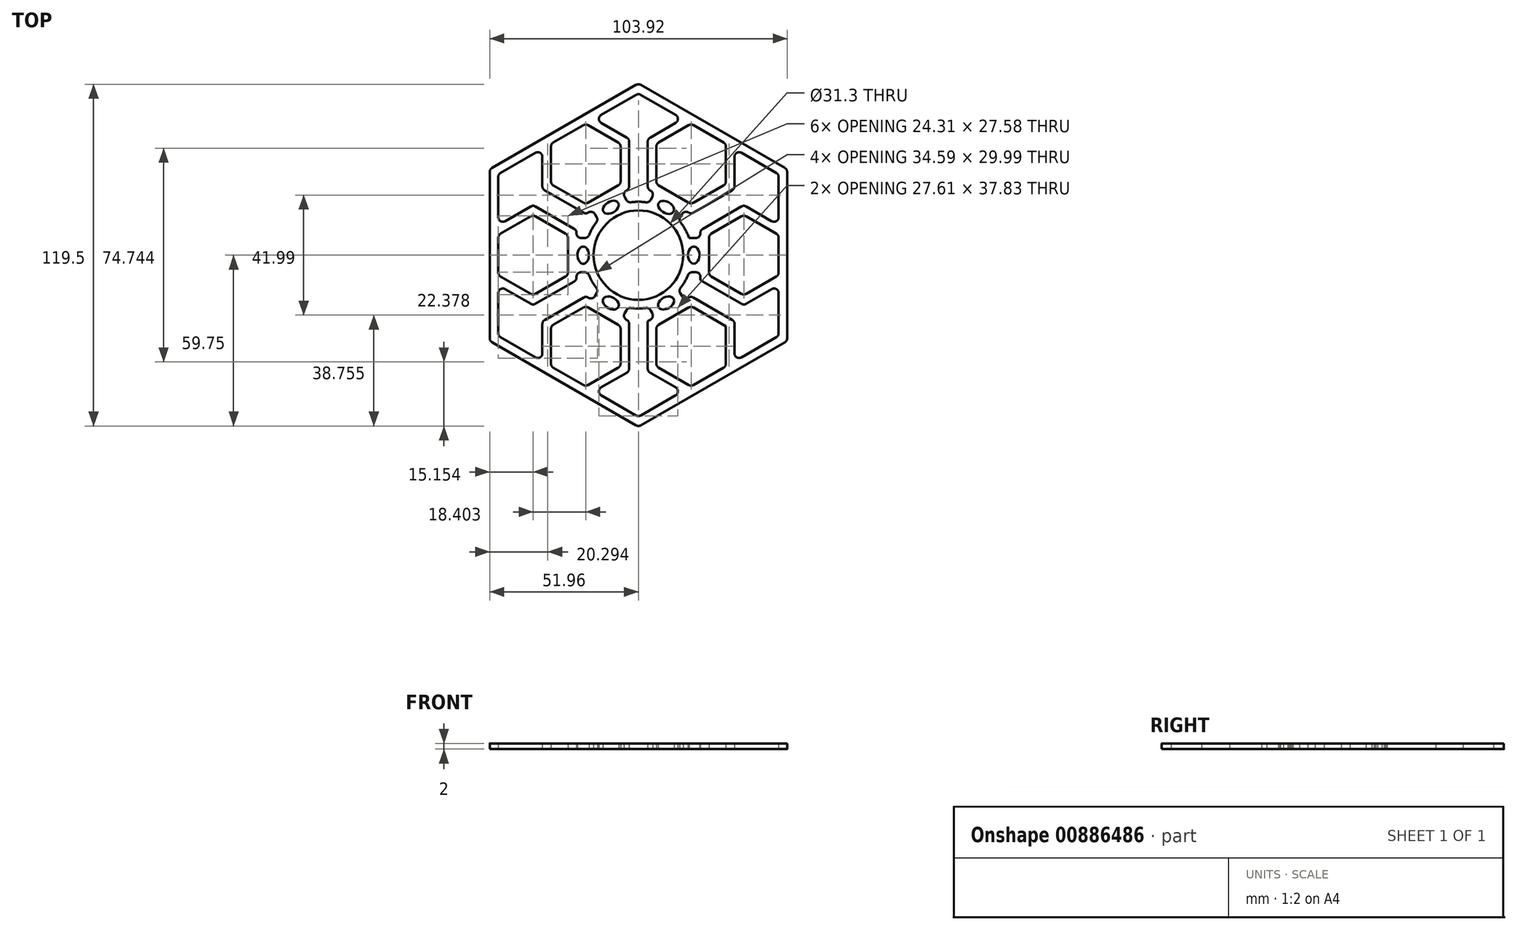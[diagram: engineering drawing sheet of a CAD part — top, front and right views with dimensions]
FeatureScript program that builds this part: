
annotation { "Feature Type Name" : "Feature", "Feature Type Description" : "" }
export const myFeature = defineFeature(function(context is Context, id is Id, definition is map)
    precondition{}
    {
        {
            var Q0;
            Q0=qCreatedBy(makeId("Top.planeOp"),FACE);
            var sketch = newSketch(context, id + "F0", { "sketchPlane" : qUnion([Q0])});
            skCircle(sketch, "E0.cCircle", {"center": v(0, 0) * mm, "radius": 60 * mm, "construction": true});
            skLineSegment(sketch, "E0.0", {"start": v(0, -60) * mm, "end": v(-51.96, -30) * mm});
            skLineSegment(sketch, "E0.1", {"start": v(-51.96, -30) * mm, "end": v(-51.96, 30) * mm});
            skLineSegment(sketch, "E0.2", {"start": v(-51.96, 30) * mm, "end": v(0, 60) * mm});
            skLineSegment(sketch, "E0.3", {"start": v(0, 60) * mm, "end": v(51.96, 30) * mm});
            skLineSegment(sketch, "E0.4", {"start": v(51.96, 30) * mm, "end": v(51.96, -30) * mm});
            skLineSegment(sketch, "E0.5", {"start": v(51.96, -30) * mm, "end": v(0, -60) * mm});
            skCircle(sketch, "E1.cCircle", {"center": v(0, 0) * mm, "radius": 56.54 * mm, "construction": true});
            skLineSegment(sketch, "E1.0", {"start": v(0, -56.54) * mm, "end": v(-15.4, -47.64) * mm});
            skLineSegment(sketch, "E1.1", {"start": v(-48.96, -28.27) * mm, "end": v(-48.96, 28.27) * mm});
            skLineSegment(sketch, "E1.2", {"start": v(-48.96, 28.27) * mm, "end": v(-18.4, 45.91) * mm});
            skLineSegment(sketch, "E1.3", {"start": v(0, 56.54) * mm, "end": v(15.4, 47.64) * mm});
            skLineSegment(sketch, "E1.4", {"start": v(48.96, 28.27) * mm, "end": v(48.96, 10.48) * mm});
            skLineSegment(sketch, "E1.5", {"start": v(48.96, -28.27) * mm, "end": v(33.56, -37.16) * mm});
            skCircle(sketch, "E2.cCircle", {"center": v(-36.8, 0) * mm, "radius": 17.5 * mm, "construction": true});
            skLineSegment(sketch, "E2.0", {"start": v(-51.96, -8.75) * mm, "end": v(-51.96, 8.75) * mm});
            skLineSegment(sketch, "E2.1", {"start": v(-48.96, 10.48) * mm, "end": v(-36.8, 17.5) * mm});
            skLineSegment(sketch, "E2.2", {"start": v(-36.8, 17.5) * mm, "end": v(-21.65, 8.75) * mm});
            skLineSegment(sketch, "E2.3", {"start": v(-21.65, 8.75) * mm, "end": v(-21.65, 6) * mm});
            skLineSegment(sketch, "E2.4", {"start": v(-21.65, -8.75) * mm, "end": v(-36.8, -17.5) * mm});
            skLineSegment(sketch, "E2.5", {"start": v(-36.8, -17.5) * mm, "end": v(-48.96, -10.48) * mm});
            skCircle(sketch, "E3.cCircle", {"center": v(-36.8, 0) * mm, "radius": 14.04 * mm, "construction": true});
            skLineSegment(sketch, "E3.0", {"start": v(-36.8, -14.04) * mm, "end": v(-48.96, -7.02) * mm});
            skLineSegment(sketch, "E3.1", {"start": v(-48.96, -7.02) * mm, "end": v(-48.96, 7.02) * mm});
            skLineSegment(sketch, "E3.2", {"start": v(-48.96, 7.02) * mm, "end": v(-36.8, 14.04) * mm});
            skLineSegment(sketch, "E3.3", {"start": v(-36.8, 14.04) * mm, "end": v(-24.65, 7.02) * mm});
            skLineSegment(sketch, "E3.4", {"start": v(-24.65, 7.02) * mm, "end": v(-24.65, -7.02) * mm});
            skLineSegment(sketch, "E3.5", {"start": v(-24.65, -7.02) * mm, "end": v(-36.8, -14.04) * mm});
            skArc(sketch, "E4", {"start": v(-17.66, -6) * mm, "mid": v(-16.15, -9.33) * mm, "end": v(-14.03, -12.3) * mm});
            skCircle(sketch, "E5", {"center": v(0, 0) * mm, "radius": 15.65 * mm});
            skLineSegment(sketch, "E6", {"start": v(-21.65, -6) * mm, "end": v(-17.66, -6) * mm});
            skLineSegment(sketch, "E7", {"start": v(-21.65, 6) * mm, "end": v(-17.66, 6) * mm});
            skLineSegment(sketch, "E8.trimOffspring", {"start": v(-21.65, -6) * mm, "end": v(-21.65, -8.75) * mm});
            skEllipse(sketch, "E9", {"center": v(-19.3, 0) * mm, "majorRadius": 3 * mm, "minorRadius": 2 * mm, "majorAxis": v(0, 1)});
            skLineSegment(sketch, "E10.1.0", {"start": v(-5.63, -21.75) * mm, "end": v(-3.25, -23.12) * mm});
            skLineSegment(sketch, "E10.1.1", {"start": v(-5.63, -21.75) * mm, "end": v(-3.63, -18.3) * mm});
            skLineSegment(sketch, "E10.1.2", {"start": v(-3.25, -23.12) * mm, "end": v(-3.25, -40.63) * mm});
            skLineSegment(sketch, "E10.1.3", {"start": v(-3.25, -40.62) * mm, "end": v(-15.4, -47.64) * mm});
            skLineSegment(sketch, "E10.1.4", {"start": v(-6.25, -38.9) * mm, "end": v(-18.4, -45.91) * mm});
            skLineSegment(sketch, "E10.1.5", {"start": v(-30.56, -38.9) * mm, "end": v(-30.56, -24.86) * mm});
            skLineSegment(sketch, "E10.1.6", {"start": v(-30.56, -24.86) * mm, "end": v(-18.4, -17.84) * mm});
            skLineSegment(sketch, "E10.1.7", {"start": v(-18.4, -17.84) * mm, "end": v(-6.25, -24.86) * mm});
            skLineSegment(sketch, "E10.1.8", {"start": v(-6.25, -24.86) * mm, "end": v(-6.25, -38.9) * mm});
            skLineSegment(sketch, "E10.1.9", {"start": v(-18.4, -14.37) * mm, "end": v(-16.02, -15.75) * mm});
            skLineSegment(sketch, "E10.1.10", {"start": v(-33.56, -23.12) * mm, "end": v(-18.4, -14.38) * mm});
            skLineSegment(sketch, "E10.1.11", {"start": v(-33.56, -37.16) * mm, "end": v(-33.56, -23.12) * mm});
            skLineSegment(sketch, "E10.1.12", {"start": v(-16.02, -15.75) * mm, "end": v(-14.03, -12.3) * mm});
            skEllipse(sketch, "E10.1.13", {"center": v(-9.65, -16.72) * mm, "majorRadius": 3 * mm, "minorRadius": 2 * mm, "majorAxis": v(-0.87, 0.5)});
            skLineSegment(sketch, "E10.2.0", {"start": v(16.02, -15.75) * mm, "end": v(18.4, -14.38) * mm});
            skLineSegment(sketch, "E10.2.1", {"start": v(16.02, -15.75) * mm, "end": v(14.03, -12.3) * mm});
            skLineSegment(sketch, "E10.2.2", {"start": v(18.4, -14.38) * mm, "end": v(33.56, -23.13) * mm});
            skLineSegment(sketch, "E10.2.3", {"start": v(33.56, -23.13) * mm, "end": v(33.56, -37.16) * mm});
            skLineSegment(sketch, "E10.2.4", {"start": v(30.56, -24.86) * mm, "end": v(30.56, -38.9) * mm});
            skLineSegment(sketch, "E10.2.5", {"start": v(18.4, -45.91) * mm, "end": v(6.25, -38.9) * mm});
            skLineSegment(sketch, "E10.2.6", {"start": v(6.25, -38.9) * mm, "end": v(6.25, -24.86) * mm});
            skLineSegment(sketch, "E10.2.7", {"start": v(6.25, -24.86) * mm, "end": v(18.4, -17.84) * mm});
            skLineSegment(sketch, "E10.2.8", {"start": v(18.4, -17.84) * mm, "end": v(30.56, -24.86) * mm});
            skLineSegment(sketch, "E10.2.9", {"start": v(3.25, -23.13) * mm, "end": v(5.63, -21.75) * mm});
            skLineSegment(sketch, "E10.2.10", {"start": v(3.25, -40.62) * mm, "end": v(3.25, -23.13) * mm});
            skLineSegment(sketch, "E10.2.11", {"start": v(15.4, -47.64) * mm, "end": v(3.25, -40.63) * mm});
            skLineSegment(sketch, "E10.2.12", {"start": v(5.63, -21.75) * mm, "end": v(3.63, -18.3) * mm});
            skEllipse(sketch, "E10.2.13", {"center": v(9.65, -16.72) * mm, "majorRadius": 3 * mm, "minorRadius": 2 * mm, "majorAxis": v(-0.87, -0.5)});
            skLineSegment(sketch, "E10.3.0", {"start": v(21.65, 6) * mm, "end": v(21.65, 8.75) * mm});
            skLineSegment(sketch, "E10.3.1", {"start": v(21.65, 6) * mm, "end": v(17.66, 6) * mm});
            skLineSegment(sketch, "E10.3.2", {"start": v(21.65, 8.75) * mm, "end": v(36.8, 17.5) * mm});
            skLineSegment(sketch, "E10.3.3", {"start": v(36.8, 17.5) * mm, "end": v(48.96, 10.48) * mm});
            skLineSegment(sketch, "E10.3.4", {"start": v(36.8, 14.04) * mm, "end": v(48.96, 7.02) * mm});
            skLineSegment(sketch, "E10.3.5", {"start": v(48.96, -7.02) * mm, "end": v(36.8, -14.04) * mm});
            skLineSegment(sketch, "E10.3.6", {"start": v(36.8, -14.04) * mm, "end": v(24.65, -7.02) * mm});
            skLineSegment(sketch, "E10.3.7", {"start": v(24.65, -7.02) * mm, "end": v(24.65, 7.02) * mm});
            skLineSegment(sketch, "E10.3.8", {"start": v(24.65, 7.02) * mm, "end": v(36.8, 14.04) * mm});
            skLineSegment(sketch, "E10.3.9", {"start": v(21.65, -8.75) * mm, "end": v(21.65, -6) * mm});
            skLineSegment(sketch, "E10.3.10", {"start": v(36.8, -17.5) * mm, "end": v(21.65, -8.75) * mm});
            skLineSegment(sketch, "E10.3.11", {"start": v(48.96, -10.48) * mm, "end": v(36.8, -17.5) * mm});
            skLineSegment(sketch, "E10.3.12", {"start": v(21.65, -6) * mm, "end": v(17.66, -6) * mm});
            skEllipse(sketch, "E10.3.13", {"center": v(19.3, 0) * mm, "majorRadius": 3 * mm, "minorRadius": 2 * mm, "majorAxis": v(0, -1)});
            skLineSegment(sketch, "E10.4.0", {"start": v(5.63, 21.75) * mm, "end": v(3.25, 23.12) * mm});
            skLineSegment(sketch, "E10.4.1", {"start": v(5.63, 21.75) * mm, "end": v(3.63, 18.3) * mm});
            skLineSegment(sketch, "E10.4.2", {"start": v(3.25, 23.12) * mm, "end": v(3.25, 40.62) * mm});
            skLineSegment(sketch, "E10.4.3", {"start": v(3.25, 40.62) * mm, "end": v(15.4, 47.64) * mm});
            skLineSegment(sketch, "E10.4.4", {"start": v(6.25, 38.9) * mm, "end": v(18.4, 45.91) * mm});
            skLineSegment(sketch, "E10.4.5", {"start": v(30.56, 38.9) * mm, "end": v(30.56, 24.86) * mm});
            skLineSegment(sketch, "E10.4.6", {"start": v(30.56, 24.86) * mm, "end": v(18.4, 17.84) * mm});
            skLineSegment(sketch, "E10.4.7", {"start": v(18.4, 17.84) * mm, "end": v(6.25, 24.86) * mm});
            skLineSegment(sketch, "E10.4.8", {"start": v(6.25, 24.86) * mm, "end": v(6.25, 38.9) * mm});
            skLineSegment(sketch, "E10.4.9", {"start": v(18.4, 14.37) * mm, "end": v(16.02, 15.75) * mm});
            skLineSegment(sketch, "E10.4.10", {"start": v(33.56, 23.12) * mm, "end": v(18.4, 14.37) * mm});
            skLineSegment(sketch, "E10.4.11", {"start": v(33.56, 37.16) * mm, "end": v(33.56, 23.12) * mm});
            skLineSegment(sketch, "E10.4.12", {"start": v(16.02, 15.75) * mm, "end": v(14.03, 12.3) * mm});
            skEllipse(sketch, "E10.4.13", {"center": v(9.65, 16.72) * mm, "majorRadius": 3 * mm, "minorRadius": 2 * mm, "majorAxis": v(0.87, -0.5)});
            skLineSegment(sketch, "E10.5.0", {"start": v(-16.02, 15.75) * mm, "end": v(-18.4, 14.38) * mm});
            skLineSegment(sketch, "E10.5.1", {"start": v(-16.02, 15.75) * mm, "end": v(-14.03, 12.3) * mm});
            skLineSegment(sketch, "E10.5.2", {"start": v(-18.4, 14.38) * mm, "end": v(-33.56, 23.12) * mm});
            skLineSegment(sketch, "E10.5.3", {"start": v(-33.56, 23.12) * mm, "end": v(-33.56, 40.62) * mm});
            skLineSegment(sketch, "E10.5.4", {"start": v(-30.56, 24.86) * mm, "end": v(-30.56, 38.9) * mm});
            skLineSegment(sketch, "E10.5.5", {"start": v(-18.4, 45.91) * mm, "end": v(-6.25, 38.9) * mm});
            skLineSegment(sketch, "E10.5.6", {"start": v(-6.25, 38.9) * mm, "end": v(-6.25, 24.86) * mm});
            skLineSegment(sketch, "E10.5.7", {"start": v(-6.25, 24.86) * mm, "end": v(-18.4, 17.84) * mm});
            skLineSegment(sketch, "E10.5.8", {"start": v(-18.4, 17.84) * mm, "end": v(-30.56, 24.86) * mm});
            skLineSegment(sketch, "E10.5.9", {"start": v(-3.25, 23.13) * mm, "end": v(-5.63, 21.75) * mm});
            skLineSegment(sketch, "E10.5.10", {"start": v(-3.25, 40.63) * mm, "end": v(-3.25, 23.13) * mm});
            skLineSegment(sketch, "E10.5.11", {"start": v(-15.4, 47.64) * mm, "end": v(-3.25, 40.62) * mm});
            skLineSegment(sketch, "E10.5.12", {"start": v(-5.63, 21.75) * mm, "end": v(-3.63, 18.3) * mm});
            skEllipse(sketch, "E10.5.13", {"center": v(-9.65, 16.72) * mm, "majorRadius": 3 * mm, "minorRadius": 2 * mm, "majorAxis": v(0.87, 0.5)});
            skLineSegment(sketch, "E11.trimOffspring", {"start": v(-33.56, -37.16) * mm, "end": v(-48.96, -28.27) * mm});
            skPoint(sketch, "E12.orphan", {"position": v(-33.56, -40.62) * mm});
            skPoint(sketch, "E13.orphan", {"position": v(-18.4, -49.37) * mm});
            skLineSegment(sketch, "E14.trimOffspring", {"start": v(-18.4, -45.91) * mm, "end": v(-30.56, -38.9) * mm});
            skPoint(sketch, "E15.orphan", {"position": v(18.4, -49.38) * mm});
            skLineSegment(sketch, "E16.trimOffspring", {"start": v(15.4, -47.64) * mm, "end": v(0, -56.54) * mm});
            skLineSegment(sketch, "E17.trimOffspring", {"start": v(30.56, -38.9) * mm, "end": v(18.4, -45.91) * mm});
            skPoint(sketch, "E18.orphan", {"position": v(33.56, -40.63) * mm});
            skArc(sketch, "E19.trimOffspring", {"start": v(-14.03, 12.3) * mm, "mid": v(-16.15, 9.33) * mm, "end": v(-17.66, 6) * mm});
            skArc(sketch, "E20.trimOffspring", {"start": v(3.63, 18.3) * mm, "mid": v(0, 18.65) * mm, "end": v(-3.63, 18.3) * mm});
            skArc(sketch, "E21.trimOffspring", {"start": v(17.66, 6) * mm, "mid": v(16.15, 9.33) * mm, "end": v(14.03, 12.3) * mm});
            skArc(sketch, "E22.trimOffspring", {"start": v(14.03, -12.3) * mm, "mid": v(16.15, -9.33) * mm, "end": v(17.66, -6) * mm});
            skArc(sketch, "E23.trimOffspring", {"start": v(-3.63, -18.3) * mm, "mid": v(1.7, -18.57) * mm, "end": v(6.88, -17.34) * mm});
            skLineSegment(sketch, "E24.trimOffspring", {"start": v(-15.4, 47.64) * mm, "end": v(0, 56.54) * mm});
            skPoint(sketch, "E25.orphan", {"position": v(-18.4, 49.37) * mm});
            skPoint(sketch, "E26.orphan", {"position": v(18.4, 49.37) * mm});
            skLineSegment(sketch, "E27.trimOffspring", {"start": v(18.4, 45.91) * mm, "end": v(30.56, 38.9) * mm});
            skLineSegment(sketch, "E28.trimOffspring", {"start": v(33.56, 37.16) * mm, "end": v(48.96, 28.27) * mm});
            skPoint(sketch, "E29.orphan", {"position": v(33.56, 40.62) * mm});
            skPoint(sketch, "E30.orphan", {"position": v(51.96, 8.75) * mm});
            skLineSegment(sketch, "E31.trimOffspring", {"start": v(48.96, 7.02) * mm, "end": v(48.96, -7.02) * mm});
            skPoint(sketch, "E32.orphan", {"position": v(51.96, -8.75) * mm});
            skLineSegment(sketch, "E33.trimOffspring", {"start": v(48.96, -10.48) * mm, "end": v(48.96, -28.27) * mm});
            skSolve(sketch);
        }
        {
            var Q0;
            {var subQ16=sQuery(id+"F0.wireOp",EDGE,"E0.0");Q0=makeQuery(id+"F0.imprint","IMPRINT",FACE,{"disambiguationData":[TD([[makeQuery(id+"F0.imprint","IMPRINT",EDGE,{"derivedFrom":subQ16}),-1.0]])]});}
            extrude(context, id + "F1", {"entities" : qUnion([Q0]), "depth" : 2 * mm, "offsetDistance" : 25 * mm});
        }
        {
            var Q0;
            Q0=makeQuery(id+"F1.opExtrude","SWEPT_EDGE",EDGE,{"disambiguationData":[OSD([sQuery(id+"F0.wireOp",EDGE,"E6"),sQuery(id+"F0.wireOp",EDGE,"E8.trimOffspring")])]});
            var Q1;
            Q1=makeQuery(id+"F1.opExtrude","SWEPT_EDGE",EDGE,{"disambiguationData":[OSD([sQuery(id+"F0.wireOp",EDGE,"E10.2.1"),sQuery(id+"F0.wireOp",EDGE,"E22.trimOffspring")])]});
            var Q2;
            Q2=makeQuery(id+"F1.opExtrude","SWEPT_EDGE",EDGE,{"disambiguationData":[OSD([sQuery(id+"F0.wireOp",EDGE,"E10.4.12"),sQuery(id+"F0.wireOp",EDGE,"E21.trimOffspring")])]});
            var Q3;
            Q3=makeQuery(id+"F1.opExtrude","SWEPT_EDGE",EDGE,{"disambiguationData":[OSD([sQuery(id+"F0.wireOp",EDGE,"E10.5.9"),sQuery(id+"F0.wireOp",EDGE,"E10.5.12")])]});
            var Q4;
            Q4=makeQuery(id+"F1.opExtrude","SWEPT_EDGE",EDGE,{"disambiguationData":[OSD([sQuery(id+"F0.wireOp",EDGE,"E10.3.12"),sQuery(id+"F0.wireOp",EDGE,"E22.trimOffspring")])]});
            var Q5;
            Q5=makeQuery(id+"F1.opExtrude","SWEPT_EDGE",EDGE,{"disambiguationData":[OSD([sQuery(id+"F0.wireOp",EDGE,"E10.5.0"),sQuery(id+"F0.wireOp",EDGE,"E10.5.1")])]});
            var Q6;
            Q6=makeQuery(id+"F1.opExtrude","SWEPT_EDGE",EDGE,{"disambiguationData":[OSD([sQuery(id+"F0.wireOp",EDGE,"E2.3"),sQuery(id+"F0.wireOp",EDGE,"E7")])]});
            var Q7;
            Q7=makeQuery(id+"F1.opExtrude","SWEPT_EDGE",EDGE,{"disambiguationData":[OSD([sQuery(id+"F0.wireOp",EDGE,"E10.1.9"),sQuery(id+"F0.wireOp",EDGE,"E10.1.12")])]});
            var Q8;
            Q8=makeQuery(id+"F1.opExtrude","SWEPT_EDGE",EDGE,{"disambiguationData":[OSD([sQuery(id+"F0.wireOp",EDGE,"E10.4.1"),sQuery(id+"F0.wireOp",EDGE,"E20.trimOffspring")])]});
            var Q9;
            Q9=makeQuery(id+"F1.opExtrude","SWEPT_EDGE",EDGE,{"disambiguationData":[OSD([sQuery(id+"F0.wireOp",EDGE,"E10.5.1"),sQuery(id+"F0.wireOp",EDGE,"E19.trimOffspring")])]});
            var Q10;
            Q10=makeQuery(id+"F1.opExtrude","SWEPT_EDGE",EDGE,{"disambiguationData":[OSD([sQuery(id+"F0.wireOp",EDGE,"E7"),sQuery(id+"F0.wireOp",EDGE,"E19.trimOffspring")])]});
            var Q11;
            Q11=makeQuery(id+"F1.opExtrude","SWEPT_EDGE",EDGE,{"disambiguationData":[OSD([sQuery(id+"F0.wireOp",EDGE,"E4"),sQuery(id+"F0.wireOp",EDGE,"E6")])]});
            var Q12;
            Q12=makeQuery(id+"F1.opExtrude","SWEPT_EDGE",EDGE,{"disambiguationData":[OSD([sQuery(id+"F0.wireOp",EDGE,"E4"),sQuery(id+"F0.wireOp",EDGE,"E10.1.12")])]});
            var Q13;
            Q13=makeQuery(id+"F1.opExtrude","SWEPT_EDGE",EDGE,{"disambiguationData":[OSD([sQuery(id+"F0.wireOp",EDGE,"E10.1.1"),sQuery(id+"F0.wireOp",EDGE,"E23.trimOffspring")])]});
            var Q14;
            Q14=makeQuery(id+"F1.opExtrude","SWEPT_EDGE",EDGE,{"disambiguationData":[OSD([sQuery(id+"F0.wireOp",EDGE,"E10.2.12"),sQuery(id+"F0.wireOp",EDGE,"E23.trimOffspring")])]});
            var Q15;
            Q15=makeQuery(id+"F1.opExtrude","SWEPT_EDGE",EDGE,{"disambiguationData":[OSD([sQuery(id+"F0.wireOp",EDGE,"E10.2.9"),sQuery(id+"F0.wireOp",EDGE,"E10.2.12")])]});
            var Q16;
            Q16=makeQuery(id+"F1.opExtrude","SWEPT_EDGE",EDGE,{"disambiguationData":[OSD([sQuery(id+"F0.wireOp",EDGE,"E10.3.9"),sQuery(id+"F0.wireOp",EDGE,"E10.3.12")])]});
            var Q17;
            Q17=makeQuery(id+"F1.opExtrude","SWEPT_EDGE",EDGE,{"disambiguationData":[OSD([sQuery(id+"F0.wireOp",EDGE,"E10.2.0"),sQuery(id+"F0.wireOp",EDGE,"E10.2.1")])]});
            var Q18;
            Q18=makeQuery(id+"F1.opExtrude","SWEPT_EDGE",EDGE,{"disambiguationData":[OSD([sQuery(id+"F0.wireOp",EDGE,"E10.4.9"),sQuery(id+"F0.wireOp",EDGE,"E10.4.12")])]});
            var Q19;
            Q19=makeQuery(id+"F1.opExtrude","SWEPT_EDGE",EDGE,{"disambiguationData":[OSD([sQuery(id+"F0.wireOp",EDGE,"E10.3.0"),sQuery(id+"F0.wireOp",EDGE,"E10.3.1")])]});
            var Q20;
            Q20=makeQuery(id+"F1.opExtrude","SWEPT_EDGE",EDGE,{"disambiguationData":[OSD([sQuery(id+"F0.wireOp",EDGE,"E10.5.12"),sQuery(id+"F0.wireOp",EDGE,"E20.trimOffspring")])]});
            var Q21;
            Q21=makeQuery(id+"F1.opExtrude","SWEPT_EDGE",EDGE,{"disambiguationData":[OSD([sQuery(id+"F0.wireOp",EDGE,"E10.4.0"),sQuery(id+"F0.wireOp",EDGE,"E10.4.1")])]});
            var Q22;
            Q22=makeQuery(id+"F1.opExtrude","SWEPT_EDGE",EDGE,{"disambiguationData":[OSD([sQuery(id+"F0.wireOp",EDGE,"E10.5.0"),sQuery(id+"F0.wireOp",EDGE,"E10.5.2")])]});
            var Q23;
            Q23=makeQuery(id+"F1.opExtrude","SWEPT_EDGE",EDGE,{"disambiguationData":[OSD([sQuery(id+"F0.wireOp",EDGE,"E10.5.2"),sQuery(id+"F0.wireOp",EDGE,"E10.5.3")])]});
            var Q24;
            Q24=makeQuery(id+"F1.opExtrude","SWEPT_EDGE",EDGE,{"disambiguationData":[OSD([sQuery(id+"F0.wireOp",EDGE,"E1.2"),sQuery(id+"F0.wireOp",EDGE,"E10.5.3")])]});
            var Q25;
            Q25=makeQuery(id+"F1.opExtrude","SWEPT_EDGE",EDGE,{"disambiguationData":[OSD([sQuery(id+"F0.wireOp",EDGE,"E1.1"),sQuery(id+"F0.wireOp",EDGE,"E1.2")])]});
            var Q26;
            Q26=makeQuery(id+"F1.opExtrude","SWEPT_EDGE",EDGE,{"disambiguationData":[OSD([sQuery(id+"F0.wireOp",EDGE,"E10.5.4"),sQuery(id+"F0.wireOp",EDGE,"E10.5.8")])]});
            var Q27;
            Q27=makeQuery(id+"F1.opExtrude","SWEPT_EDGE",EDGE,{"disambiguationData":[OSD([sQuery(id+"F0.wireOp",EDGE,"E10.5.10"),sQuery(id+"F0.wireOp",EDGE,"E10.5.11")])]});
            var Q28;
            Q28=makeQuery(id+"F1.opExtrude","SWEPT_EDGE",EDGE,{"disambiguationData":[OSD([sQuery(id+"F0.wireOp",EDGE,"E10.5.9"),sQuery(id+"F0.wireOp",EDGE,"E10.5.10")])]});
            var Q29;
            Q29=makeQuery(id+"F1.opExtrude","SWEPT_EDGE",EDGE,{"disambiguationData":[OSD([sQuery(id+"F0.wireOp",EDGE,"E10.5.5"),sQuery(id+"F0.wireOp",EDGE,"E10.5.6")])]});
            var Q30;
            Q30=makeQuery(id+"F1.opExtrude","SWEPT_EDGE",EDGE,{"disambiguationData":[OSD([sQuery(id+"F0.wireOp",EDGE,"E10.5.6"),sQuery(id+"F0.wireOp",EDGE,"E10.5.7")])]});
            var Q31;
            Q31=makeQuery(id+"F1.opExtrude","SWEPT_EDGE",EDGE,{"disambiguationData":[OSD([sQuery(id+"F0.wireOp",EDGE,"E10.5.7"),sQuery(id+"F0.wireOp",EDGE,"E10.5.8")])]});
            var Q32;
            Q32=makeQuery(id+"F1.opExtrude","SWEPT_EDGE",EDGE,{"disambiguationData":[OSD([sQuery(id+"F0.wireOp",EDGE,"E1.2"),sQuery(id+"F0.wireOp",EDGE,"E10.5.4")])]});
            var Q33;
            Q33=makeQuery(id+"F1.opExtrude","SWEPT_EDGE",EDGE,{"disambiguationData":[OSD([sQuery(id+"F0.wireOp",EDGE,"E1.2"),sQuery(id+"F0.wireOp",EDGE,"E10.5.5")])]});
            var Q34;
            Q34=makeQuery(id+"F1.opExtrude","SWEPT_EDGE",EDGE,{"disambiguationData":[OSD([sQuery(id+"F0.wireOp",EDGE,"E10.5.11"),sQuery(id+"F0.wireOp",EDGE,"E24.trimOffspring")])]});
            var Q35;
            Q35=makeQuery(id+"F1.opExtrude","SWEPT_EDGE",EDGE,{"disambiguationData":[OSD([sQuery(id+"F0.wireOp",EDGE,"E0.1"),sQuery(id+"F0.wireOp",EDGE,"E0.2")])]});
            var Q36;
            Q36=makeQuery(id+"F1.opExtrude","SWEPT_EDGE",EDGE,{"disambiguationData":[OSD([sQuery(id+"F0.wireOp",EDGE,"E0.2"),sQuery(id+"F0.wireOp",EDGE,"E0.3")])]});
            var Q37;
            Q37=makeQuery(id+"F1.opExtrude","SWEPT_EDGE",EDGE,{"disambiguationData":[OSD([sQuery(id+"F0.wireOp",EDGE,"E0.0"),sQuery(id+"F0.wireOp",EDGE,"E0.1")])]});
            var Q38;
            Q38=makeQuery(id+"F1.opExtrude","SWEPT_EDGE",EDGE,{"disambiguationData":[OSD([sQuery(id+"F0.wireOp",EDGE,"E0.0"),sQuery(id+"F0.wireOp",EDGE,"E0.5")])]});
            var Q39;
            Q39=makeQuery(id+"F1.opExtrude","SWEPT_EDGE",EDGE,{"disambiguationData":[OSD([sQuery(id+"F0.wireOp",EDGE,"E0.4"),sQuery(id+"F0.wireOp",EDGE,"E0.5")])]});
            var Q40;
            Q40=makeQuery(id+"F1.opExtrude","SWEPT_EDGE",EDGE,{"disambiguationData":[OSD([sQuery(id+"F0.wireOp",EDGE,"E0.3"),sQuery(id+"F0.wireOp",EDGE,"E0.4")])]});
            var Q41;
            Q41=makeQuery(id+"F1.opExtrude","SWEPT_EDGE",EDGE,{"disambiguationData":[OSD([sQuery(id+"F0.wireOp",EDGE,"E1.0"),sQuery(id+"F0.wireOp",EDGE,"E16.trimOffspring")])]});
            var Q42;
            Q42=makeQuery(id+"F1.opExtrude","SWEPT_EDGE",EDGE,{"disambiguationData":[OSD([sQuery(id+"F0.wireOp",EDGE,"E10.1.5"),sQuery(id+"F0.wireOp",EDGE,"E14.trimOffspring")])]});
            var Q43;
            Q43=makeQuery(id+"F1.opExtrude","SWEPT_EDGE",EDGE,{"disambiguationData":[OSD([sQuery(id+"F0.wireOp",EDGE,"E1.1"),sQuery(id+"F0.wireOp",EDGE,"E11.trimOffspring")])]});
            var Q44;
            Q44=makeQuery(id+"F1.opExtrude","SWEPT_EDGE",EDGE,{"disambiguationData":[OSD([sQuery(id+"F0.wireOp",EDGE,"E3.0"),sQuery(id+"F0.wireOp",EDGE,"E3.1")])]});
            var Q45;
            Q45=makeQuery(id+"F1.opExtrude","SWEPT_EDGE",EDGE,{"disambiguationData":[OSD([sQuery(id+"F0.wireOp",EDGE,"E1.1"),sQuery(id+"F0.wireOp",EDGE,"E2.1")])]});
            var Q46;
            Q46=makeQuery(id+"F1.opExtrude","SWEPT_EDGE",EDGE,{"disambiguationData":[OSD([sQuery(id+"F0.wireOp",EDGE,"E10.4.4"),sQuery(id+"F0.wireOp",EDGE,"E10.4.8")])]});
            var Q47;
            Q47=makeQuery(id+"F1.opExtrude","SWEPT_EDGE",EDGE,{"disambiguationData":[OSD([sQuery(id+"F0.wireOp",EDGE,"E10.4.7"),sQuery(id+"F0.wireOp",EDGE,"E10.4.8")])]});
            var Q48;
            Q48=makeQuery(id+"F1.opExtrude","SWEPT_EDGE",EDGE,{"disambiguationData":[OSD([sQuery(id+"F0.wireOp",EDGE,"E10.3.7"),sQuery(id+"F0.wireOp",EDGE,"E10.3.8")])]});
            var Q49;
            Q49=makeQuery(id+"F1.opExtrude","SWEPT_EDGE",EDGE,{"disambiguationData":[OSD([sQuery(id+"F0.wireOp",EDGE,"E3.1"),sQuery(id+"F0.wireOp",EDGE,"E3.2")])]});
            var Q50;
            Q50=makeQuery(id+"F1.opExtrude","SWEPT_EDGE",EDGE,{"disambiguationData":[OSD([sQuery(id+"F0.wireOp",EDGE,"E10.3.6"),sQuery(id+"F0.wireOp",EDGE,"E10.3.7")])]});
            var Q51;
            Q51=makeQuery(id+"F1.opExtrude","SWEPT_EDGE",EDGE,{"disambiguationData":[OSD([sQuery(id+"F0.wireOp",EDGE,"E10.4.10"),sQuery(id+"F0.wireOp",EDGE,"E10.4.11")])]});
            var Q52;
            Q52=makeQuery(id+"F1.opExtrude","SWEPT_EDGE",EDGE,{"disambiguationData":[OSD([sQuery(id+"F0.wireOp",EDGE,"E10.3.10"),sQuery(id+"F0.wireOp",EDGE,"E10.3.11")])]});
            var Q53;
            Q53=makeQuery(id+"F1.opExtrude","SWEPT_EDGE",EDGE,{"disambiguationData":[OSD([sQuery(id+"F0.wireOp",EDGE,"E10.2.2"),sQuery(id+"F0.wireOp",EDGE,"E10.2.3")])]});
            var Q54;
            Q54=makeQuery(id+"F1.opExtrude","SWEPT_EDGE",EDGE,{"disambiguationData":[OSD([sQuery(id+"F0.wireOp",EDGE,"E10.1.2"),sQuery(id+"F0.wireOp",EDGE,"E10.1.3")])]});
            var Q55;
            Q55=makeQuery(id+"F1.opExtrude","SWEPT_EDGE",EDGE,{"disambiguationData":[OSD([sQuery(id+"F0.wireOp",EDGE,"E10.2.10"),sQuery(id+"F0.wireOp",EDGE,"E10.2.11")])]});
            var Q56;
            Q56=makeQuery(id+"F1.opExtrude","SWEPT_EDGE",EDGE,{"disambiguationData":[OSD([sQuery(id+"F0.wireOp",EDGE,"E10.3.4"),sQuery(id+"F0.wireOp",EDGE,"E10.3.8")])]});
            var Q57;
            Q57=makeQuery(id+"F1.opExtrude","SWEPT_EDGE",EDGE,{"disambiguationData":[OSD([sQuery(id+"F0.wireOp",EDGE,"E10.2.7"),sQuery(id+"F0.wireOp",EDGE,"E10.2.8")])]});
            var Q58;
            Q58=makeQuery(id+"F1.opExtrude","SWEPT_EDGE",EDGE,{"disambiguationData":[OSD([sQuery(id+"F0.wireOp",EDGE,"E10.2.6"),sQuery(id+"F0.wireOp",EDGE,"E10.2.7")])]});
            var Q59;
            Q59=makeQuery(id+"F1.opExtrude","SWEPT_EDGE",EDGE,{"disambiguationData":[OSD([sQuery(id+"F0.wireOp",EDGE,"E10.1.5"),sQuery(id+"F0.wireOp",EDGE,"E10.1.6")])]});
            var Q60;
            Q60=makeQuery(id+"F1.opExtrude","SWEPT_EDGE",EDGE,{"disambiguationData":[OSD([sQuery(id+"F0.wireOp",EDGE,"E2.4"),sQuery(id+"F0.wireOp",EDGE,"E8.trimOffspring")])]});
            var Q61;
            Q61=makeQuery(id+"F1.opExtrude","SWEPT_EDGE",EDGE,{"disambiguationData":[OSD([sQuery(id+"F0.wireOp",EDGE,"E2.2"),sQuery(id+"F0.wireOp",EDGE,"E2.3")])]});
            var Q62;
            Q62=makeQuery(id+"F1.opExtrude","SWEPT_EDGE",EDGE,{"disambiguationData":[OSD([sQuery(id+"F0.wireOp",EDGE,"E10.4.9"),sQuery(id+"F0.wireOp",EDGE,"E10.4.10")])]});
            var Q63;
            Q63=makeQuery(id+"F1.opExtrude","SWEPT_EDGE",EDGE,{"disambiguationData":[OSD([sQuery(id+"F0.wireOp",EDGE,"E10.1.0"),sQuery(id+"F0.wireOp",EDGE,"E10.1.2")])]});
            var Q64;
            Q64=makeQuery(id+"F1.opExtrude","SWEPT_EDGE",EDGE,{"disambiguationData":[OSD([sQuery(id+"F0.wireOp",EDGE,"E10.2.0"),sQuery(id+"F0.wireOp",EDGE,"E10.2.2")])]});
            var Q65;
            Q65=makeQuery(id+"F1.opExtrude","SWEPT_EDGE",EDGE,{"disambiguationData":[OSD([sQuery(id+"F0.wireOp",EDGE,"E10.3.2"),sQuery(id+"F0.wireOp",EDGE,"E10.3.3")])]});
            var Q66;
            Q66=makeQuery(id+"F1.opExtrude","SWEPT_EDGE",EDGE,{"disambiguationData":[OSD([sQuery(id+"F0.wireOp",EDGE,"E10.3.0"),sQuery(id+"F0.wireOp",EDGE,"E10.3.2")])]});
            var Q67;
            Q67=makeQuery(id+"F1.opExtrude","SWEPT_EDGE",EDGE,{"disambiguationData":[OSD([sQuery(id+"F0.wireOp",EDGE,"E10.4.2"),sQuery(id+"F0.wireOp",EDGE,"E10.4.3")])]});
            var Q68;
            Q68=makeQuery(id+"F1.opExtrude","SWEPT_EDGE",EDGE,{"disambiguationData":[OSD([sQuery(id+"F0.wireOp",EDGE,"E10.2.5"),sQuery(id+"F0.wireOp",EDGE,"E17.trimOffspring")])]});
            var Q69;
            Q69=makeQuery(id+"F1.opExtrude","SWEPT_EDGE",EDGE,{"disambiguationData":[OSD([sQuery(id+"F0.wireOp",EDGE,"E10.2.4"),sQuery(id+"F0.wireOp",EDGE,"E17.trimOffspring")])]});
            var Q70;
            Q70=makeQuery(id+"F1.opExtrude","SWEPT_EDGE",EDGE,{"disambiguationData":[OSD([sQuery(id+"F0.wireOp",EDGE,"E1.5"),sQuery(id+"F0.wireOp",EDGE,"E33.trimOffspring")])]});
            var Q71;
            Q71=makeQuery(id+"F1.opExtrude","SWEPT_EDGE",EDGE,{"disambiguationData":[OSD([sQuery(id+"F0.wireOp",EDGE,"E10.3.5"),sQuery(id+"F0.wireOp",EDGE,"E31.trimOffspring")])]});
            var Q72;
            Q72=makeQuery(id+"F1.opExtrude","SWEPT_EDGE",EDGE,{"disambiguationData":[OSD([sQuery(id+"F0.wireOp",EDGE,"E10.4.0"),sQuery(id+"F0.wireOp",EDGE,"E10.4.2")])]});
            var Q73;
            Q73=makeQuery(id+"F1.opExtrude","SWEPT_EDGE",EDGE,{"disambiguationData":[OSD([sQuery(id+"F0.wireOp",EDGE,"E3.4"),sQuery(id+"F0.wireOp",EDGE,"E3.5")])]});
            var Q74;
            Q74=makeQuery(id+"F1.opExtrude","SWEPT_EDGE",EDGE,{"disambiguationData":[OSD([sQuery(id+"F0.wireOp",EDGE,"E10.1.4"),sQuery(id+"F0.wireOp",EDGE,"E10.1.8")])]});
            var Q75;
            Q75=makeQuery(id+"F1.opExtrude","SWEPT_EDGE",EDGE,{"disambiguationData":[OSD([sQuery(id+"F0.wireOp",EDGE,"E2.1"),sQuery(id+"F0.wireOp",EDGE,"E2.2")])]});
            var Q76;
            Q76=makeQuery(id+"F1.opExtrude","SWEPT_EDGE",EDGE,{"disambiguationData":[OSD([sQuery(id+"F0.wireOp",EDGE,"E10.4.6"),sQuery(id+"F0.wireOp",EDGE,"E10.4.7")])]});
            var Q77;
            Q77=makeQuery(id+"F1.opExtrude","SWEPT_EDGE",EDGE,{"disambiguationData":[OSD([sQuery(id+"F0.wireOp",EDGE,"E10.4.5"),sQuery(id+"F0.wireOp",EDGE,"E10.4.6")])]});
            var Q78;
            Q78=makeQuery(id+"F1.opExtrude","SWEPT_EDGE",EDGE,{"disambiguationData":[OSD([sQuery(id+"F0.wireOp",EDGE,"E1.4"),sQuery(id+"F0.wireOp",EDGE,"E10.3.3")])]});
            var Q79;
            Q79=makeQuery(id+"F1.opExtrude","SWEPT_EDGE",EDGE,{"disambiguationData":[OSD([sQuery(id+"F0.wireOp",EDGE,"E10.2.5"),sQuery(id+"F0.wireOp",EDGE,"E10.2.6")])]});
            var Q80;
            Q80=makeQuery(id+"F1.opExtrude","SWEPT_EDGE",EDGE,{"disambiguationData":[OSD([sQuery(id+"F0.wireOp",EDGE,"E10.1.6"),sQuery(id+"F0.wireOp",EDGE,"E10.1.7")])]});
            var Q81;
            Q81=makeQuery(id+"F1.opExtrude","SWEPT_EDGE",EDGE,{"disambiguationData":[OSD([sQuery(id+"F0.wireOp",EDGE,"E3.2"),sQuery(id+"F0.wireOp",EDGE,"E3.3")])]});
            var Q82;
            Q82=makeQuery(id+"F1.opExtrude","SWEPT_EDGE",EDGE,{"disambiguationData":[OSD([sQuery(id+"F0.wireOp",EDGE,"E1.3"),sQuery(id+"F0.wireOp",EDGE,"E24.trimOffspring")])]});
            var Q83;
            Q83=makeQuery(id+"F1.opExtrude","SWEPT_EDGE",EDGE,{"disambiguationData":[OSD([sQuery(id+"F0.wireOp",EDGE,"E10.4.4"),sQuery(id+"F0.wireOp",EDGE,"E27.trimOffspring")])]});
            var Q84;
            Q84=makeQuery(id+"F1.opExtrude","SWEPT_EDGE",EDGE,{"disambiguationData":[OSD([sQuery(id+"F0.wireOp",EDGE,"E10.4.5"),sQuery(id+"F0.wireOp",EDGE,"E27.trimOffspring")])]});
            var Q85;
            Q85=makeQuery(id+"F1.opExtrude","SWEPT_EDGE",EDGE,{"disambiguationData":[OSD([sQuery(id+"F0.wireOp",EDGE,"E10.1.7"),sQuery(id+"F0.wireOp",EDGE,"E10.1.8")])]});
            var Q86;
            Q86=makeQuery(id+"F1.opExtrude","SWEPT_EDGE",EDGE,{"disambiguationData":[OSD([sQuery(id+"F0.wireOp",EDGE,"E3.3"),sQuery(id+"F0.wireOp",EDGE,"E3.4")])]});
            var Q87;
            Q87=makeQuery(id+"F1.opExtrude","SWEPT_EDGE",EDGE,{"disambiguationData":[OSD([sQuery(id+"F0.wireOp",EDGE,"E1.4"),sQuery(id+"F0.wireOp",EDGE,"E28.trimOffspring")])]});
            var Q88;
            Q88=makeQuery(id+"F1.opExtrude","SWEPT_EDGE",EDGE,{"disambiguationData":[OSD([sQuery(id+"F0.wireOp",EDGE,"E1.3"),sQuery(id+"F0.wireOp",EDGE,"E10.4.3")])]});
            var Q89;
            Q89=makeQuery(id+"F1.opExtrude","SWEPT_EDGE",EDGE,{"disambiguationData":[OSD([sQuery(id+"F0.wireOp",EDGE,"E10.3.4"),sQuery(id+"F0.wireOp",EDGE,"E31.trimOffspring")])]});
            var Q90;
            Q90=makeQuery(id+"F1.opExtrude","SWEPT_EDGE",EDGE,{"disambiguationData":[OSD([sQuery(id+"F0.wireOp",EDGE,"E10.3.5"),sQuery(id+"F0.wireOp",EDGE,"E10.3.6")])]});
            var Q91;
            Q91=makeQuery(id+"F1.opExtrude","SWEPT_EDGE",EDGE,{"disambiguationData":[OSD([sQuery(id+"F0.wireOp",EDGE,"E1.5"),sQuery(id+"F0.wireOp",EDGE,"E10.2.3")])]});
            var Q92;
            Q92=makeQuery(id+"F1.opExtrude","SWEPT_EDGE",EDGE,{"disambiguationData":[OSD([sQuery(id+"F0.wireOp",EDGE,"E10.2.11"),sQuery(id+"F0.wireOp",EDGE,"E16.trimOffspring")])]});
            var Q93;
            Q93=makeQuery(id+"F1.opExtrude","SWEPT_EDGE",EDGE,{"disambiguationData":[OSD([sQuery(id+"F0.wireOp",EDGE,"E10.1.10"),sQuery(id+"F0.wireOp",EDGE,"E10.1.11")])]});
            var Q94;
            Q94=makeQuery(id+"F1.opExtrude","SWEPT_EDGE",EDGE,{"disambiguationData":[OSD([sQuery(id+"F0.wireOp",EDGE,"E10.1.4"),sQuery(id+"F0.wireOp",EDGE,"E14.trimOffspring")])]});
            var Q95;
            Q95=makeQuery(id+"F1.opExtrude","SWEPT_EDGE",EDGE,{"disambiguationData":[OSD([sQuery(id+"F0.wireOp",EDGE,"E1.1"),sQuery(id+"F0.wireOp",EDGE,"E2.5")])]});
            var Q96;
            Q96=makeQuery(id+"F1.opExtrude","SWEPT_EDGE",EDGE,{"disambiguationData":[OSD([sQuery(id+"F0.wireOp",EDGE,"E10.1.9"),sQuery(id+"F0.wireOp",EDGE,"E10.1.10")])]});
            var Q97;
            Q97=makeQuery(id+"F1.opExtrude","SWEPT_EDGE",EDGE,{"disambiguationData":[OSD([sQuery(id+"F0.wireOp",EDGE,"E10.4.11"),sQuery(id+"F0.wireOp",EDGE,"E28.trimOffspring")])]});
            var Q98;
            Q98=makeQuery(id+"F1.opExtrude","SWEPT_EDGE",EDGE,{"disambiguationData":[OSD([sQuery(id+"F0.wireOp",EDGE,"E2.4"),sQuery(id+"F0.wireOp",EDGE,"E2.5")])]});
            var Q99;
            Q99=makeQuery(id+"F1.opExtrude","SWEPT_EDGE",EDGE,{"disambiguationData":[OSD([sQuery(id+"F0.wireOp",EDGE,"E3.0"),sQuery(id+"F0.wireOp",EDGE,"E3.5")])]});
            var Q100;
            Q100=makeQuery(id+"F1.opExtrude","SWEPT_EDGE",EDGE,{"disambiguationData":[OSD([sQuery(id+"F0.wireOp",EDGE,"E10.1.0"),sQuery(id+"F0.wireOp",EDGE,"E10.1.1")])]});
            var Q101;
            Q101=makeQuery(id+"F1.opExtrude","SWEPT_EDGE",EDGE,{"disambiguationData":[OSD([sQuery(id+"F0.wireOp",EDGE,"E10.3.11"),sQuery(id+"F0.wireOp",EDGE,"E33.trimOffspring")])]});
            var Q102;
            Q102=makeQuery(id+"F1.opExtrude","SWEPT_EDGE",EDGE,{"disambiguationData":[OSD([sQuery(id+"F0.wireOp",EDGE,"E1.0"),sQuery(id+"F0.wireOp",EDGE,"E10.1.3")])]});
            var Q103;
            Q103=makeQuery(id+"F1.opExtrude","SWEPT_EDGE",EDGE,{"disambiguationData":[OSD([sQuery(id+"F0.wireOp",EDGE,"E10.1.11"),sQuery(id+"F0.wireOp",EDGE,"E11.trimOffspring")])]});
            fillet(context, id + "F2", {"entities" : qUnion([Q0, Q1, Q2, Q3, Q4, Q5, Q6, Q7, Q8, Q9, Q10, Q11, Q12, Q13, Q14, Q15, Q16, Q17, Q18, Q19, Q20, Q21, Q22, Q23, Q24, Q25, Q26, Q27, Q28, Q29, Q30, Q31, Q32, Q33, Q34, Q35, Q36, Q37, Q38, Q39, Q40, Q41, Q42, Q43, Q44, Q45, Q46, Q47, Q48, Q49, Q50, Q51, Q52, Q53, Q54, Q55, Q56, Q57, Q58, Q59, Q60, Q61, Q62, Q63, Q64, Q65, Q66, Q67, Q68, Q69, Q70, Q71, Q72, Q73, Q74, Q75, Q76, Q77, Q78, Q79, Q80, Q81, Q82, Q83, Q84, Q85, Q86, Q87, Q88, Q89, Q90, Q91, Q92, Q93, Q94, Q95, Q96, Q97, Q98, Q99, Q100, Q101, Q102, Q103]), "radius" : 1.6 * mm, "tangentPropagation" : true, "allowEdgeOverflow" : false});
        }
    });
